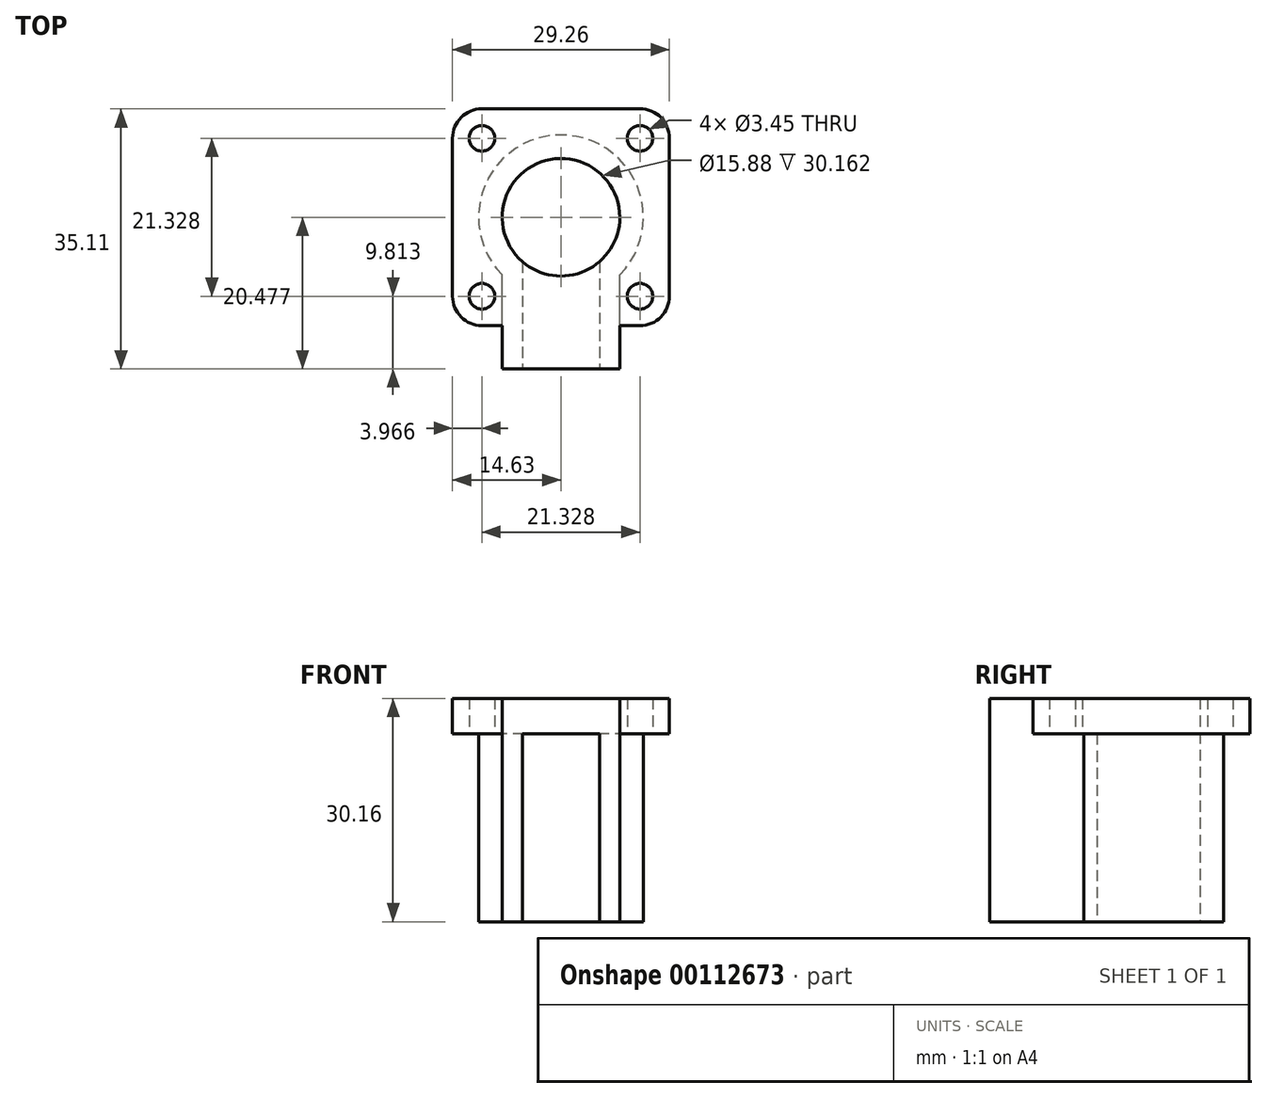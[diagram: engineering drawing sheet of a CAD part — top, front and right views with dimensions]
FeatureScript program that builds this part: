
annotation { "Feature Type Name" : "Feature", "Feature Type Description" : "" }
export const myFeature = defineFeature(function(context is Context, id is Id, definition is map)
    precondition{}
    {
        {
            var Q0;
            Q0=qCreatedBy(makeId("Top.planeOp"),FACE);
            var sketch = newSketch(context, id + "F0", { "sketchPlane" : qUnion([Q0])});
            skLineSegment(sketch, "E0.bottom", {"start": v(0, 0) * mm, "end": v(-10.4, 0) * mm, "construction": true});
            skLineSegment(sketch, "E0.top", {"start": v(0, -14.48) * mm, "end": v(-10.4, -14.48) * mm, "construction": true});
            skLineSegment(sketch, "E0.left", {"start": v(0, 0) * mm, "end": v(0, -14.48) * mm});
            skLineSegment(sketch, "E0.right", {"start": v(-10.4, 0) * mm, "end": v(-10.4, -14.48) * mm});
            skLineSegment(sketch, "E1", {"start": v(-10.4, -14.48) * mm, "end": v(-13.14, -14.48) * mm});
            skLineSegment(sketch, "E2", {"start": v(0, -14.48) * mm, "end": v(2.74, -14.48) * mm});
            skLineSegment(sketch, "E3", {"start": v(-13.14, -14.48) * mm, "end": v(-13.14, -1.78) * mm});
            skLineSegment(sketch, "E4", {"start": v(2.74, -14.48) * mm, "end": v(2.74, -1.78) * mm});
            skLineSegment(sketch, "E5", {"start": v(-5.2, 0) * mm, "end": v(-5.2, 6) * mm, "construction": true});
            skArc(sketch, "E6", {"start": v(0, 0) * mm, "mid": v(-5.2, 13.93) * mm, "end": v(-10.4, 0) * mm});
            skArc(sketch, "E7", {"start": v(2.74, -1.78) * mm, "mid": v(-5.2, 17.1) * mm, "end": v(-13.14, -1.78) * mm});
            skSolve(sketch);
        }
        {
            var Q0;
            Q0=makeQuery(id+"F0.imprint","IMPRINT",FACE,{"disambiguationData":[TD([[makeQuery(id+"F0.imprint","IMPRINT",EDGE,{"derivedFrom":sQuery(id+"F0.wireOp",EDGE,"E0.left")}),1.0]])]});
            extrude(context, id + "F1", {"entities" : qUnion([Q0]), "depth" : 25.4 * mm});
        }
        {
            var Q0;
            Q0=makeQuery(id+"F1.opExtrude","CAP_FACE",FACE,{"disambiguationData":[OSD([sQuery(id+"F0.wireOp",EDGE,"E0.left"),sQuery(id+"F0.wireOp",EDGE,"E0.right"),sQuery(id+"F0.wireOp",EDGE,"E1"),sQuery(id+"F0.wireOp",EDGE,"E2"),sQuery(id+"F0.wireOp",EDGE,"E3"),sQuery(id+"F0.wireOp",EDGE,"E4"),sQuery(id+"F0.wireOp",EDGE,"E6"),sQuery(id+"F0.wireOp",EDGE,"E7")])],"isStart":false});
            var sketch = newSketch(context, id + "F2", { "sketchPlane" : qUnion([Q0])});
            skLineSegment(sketch, "E8", {"start": v(-13.14, -14.48) * mm, "end": v(2.74, -14.48) * mm});
            skLineSegment(sketch, "E9", {"start": v(2.74, -14.48) * mm, "end": v(2.74, -8.64) * mm});
            skLineSegment(sketch, "E10", {"start": v(2.74, -8.64) * mm, "end": v(-13.14, -8.64) * mm, "construction": true});
            skLineSegment(sketch, "E11", {"start": v(-13.14, -8.64) * mm, "end": v(-13.14, -14.48) * mm});
            skLineSegment(sketch, "E12", {"start": v(-5.2, -8.64) * mm, "end": v(-5.2, 20.63) * mm, "construction": true});
            skLineSegment(sketch, "E13", {"start": v(-13.14, -8.64) * mm, "end": v(-19.83, -8.64) * mm});
            skLineSegment(sketch, "E14", {"start": v(-19.83, -8.64) * mm, "end": v(-19.83, 20.63) * mm});
            skLineSegment(sketch, "E15", {"start": v(-19.83, 20.63) * mm, "end": v(9.43, 20.63) * mm});
            skLineSegment(sketch, "E16", {"start": v(9.43, 20.63) * mm, "end": v(9.43, -8.64) * mm});
            skLineSegment(sketch, "E17", {"start": v(9.43, -8.64) * mm, "end": v(2.74, -8.64) * mm});
            skLineSegment(sketch, "E18.bottom", {"start": v(-15.86, 16.66) * mm, "end": v(5.46, 16.66) * mm, "construction": true});
            skLineSegment(sketch, "E18.top", {"start": v(-15.86, -4.67) * mm, "end": v(5.46, -4.67) * mm, "construction": true});
            skLineSegment(sketch, "E18.left", {"start": v(-15.86, 16.66) * mm, "end": v(-15.86, -4.67) * mm, "construction": true});
            skLineSegment(sketch, "E18.right", {"start": v(5.46, 16.66) * mm, "end": v(5.46, -4.67) * mm, "construction": true});
            skPoint(sketch, "E18.middle", {"position": v(-5.2, 6) * mm});
            skCircle(sketch, "E19", {"center": v(-15.86, 16.66) * mm, "radius": 3.97 * mm, "construction": true});
            skCircle(sketch, "E20", {"center": v(-15.86, -4.67) * mm, "radius": 1.73 * mm});
            skCircle(sketch, "E21", {"center": v(5.46, -4.67) * mm, "radius": 1.73 * mm});
            skCircle(sketch, "E22", {"center": v(5.46, 16.66) * mm, "radius": 1.73 * mm});
            skCircle(sketch, "E23", {"center": v(-15.86, 16.66) * mm, "radius": 1.73 * mm});
            skCircle(sketch, "E24", {"center": v(-5.2, 6) * mm, "radius": 7.94 * mm});
            skSolve(sketch);
        }
        {
            var Q0;
            {var subQ1=sQuery(id+"F2.wireOp",EDGE,"E13");Q0=makeQuery(id+"F2.imprint","IMPRINT",FACE,{"disambiguationData":[TD([[makeQuery(id+"F2.imprint","IMPRINT",EDGE,{"derivedFrom":subQ1}),-1.0]])]});}
            var Q1;
            {var subQ2=sQuery(id+"F2.wireOp",EDGE,"E9");Q1=makeQuery(id+"F2.imprint","IMPRINT",FACE,{"disambiguationData":[TD([[makeQuery(id+"F2.imprint","IMPRINT",EDGE,{"derivedFrom":subQ2}),1.0]])]});}
            var Q2;
            {var subQ1=makeQuery(id+"F1.opExtrude","CAP_EDGE",EDGE,{"disambiguationData":[OSD([sQuery(id+"F0.wireOp",EDGE,"E0.left")])],"isStart":false});Q2=makeQuery(id+"F2.imprint","IMPRINT",FACE,{"disambiguationData":[TD([[makeQuery(id+"F2.imprint","IMPRINT",EDGE,{"derivedFrom":subQ1}),-1.0]])]});}
            extrude(context, id + "F3", {"entities" : qUnion([Q0, Q1, Q2]), "operationType" : NewBodyOperationType.ADD, "depth" : 4.76 * mm});
        }
        {
            var Q0;
            Q0=makeQuery(id+"F3.opExtrude","SWEPT_EDGE",EDGE,{"disambiguationData":[OSD([sQuery(id+"F2.wireOp",EDGE,"E13"),sQuery(id+"F2.wireOp",EDGE,"E14")])]});
            var Q1;
            Q1=makeQuery(id+"F3.opExtrude","SWEPT_EDGE",EDGE,{"disambiguationData":[OSD([sQuery(id+"F2.wireOp",EDGE,"E16"),sQuery(id+"F2.wireOp",EDGE,"E17")])]});
            var Q2;
            Q2=makeQuery(id+"F3.opExtrude","SWEPT_EDGE",EDGE,{"disambiguationData":[OSD([sQuery(id+"F2.wireOp",EDGE,"E15"),sQuery(id+"F2.wireOp",EDGE,"E16")])]});
            var Q3;
            Q3=makeQuery(id+"F3.opExtrude","SWEPT_EDGE",EDGE,{"disambiguationData":[OSD([sQuery(id+"F2.wireOp",EDGE,"E14"),sQuery(id+"F2.wireOp",EDGE,"E15")])]});
            fillet(context, id + "F4", {"entities" : qUnion([Q0, Q1, Q2, Q3]), "radius" : 3.97 * mm, "tangentPropagation" : true, "allowEdgeOverflow" : false});
        }
    });
